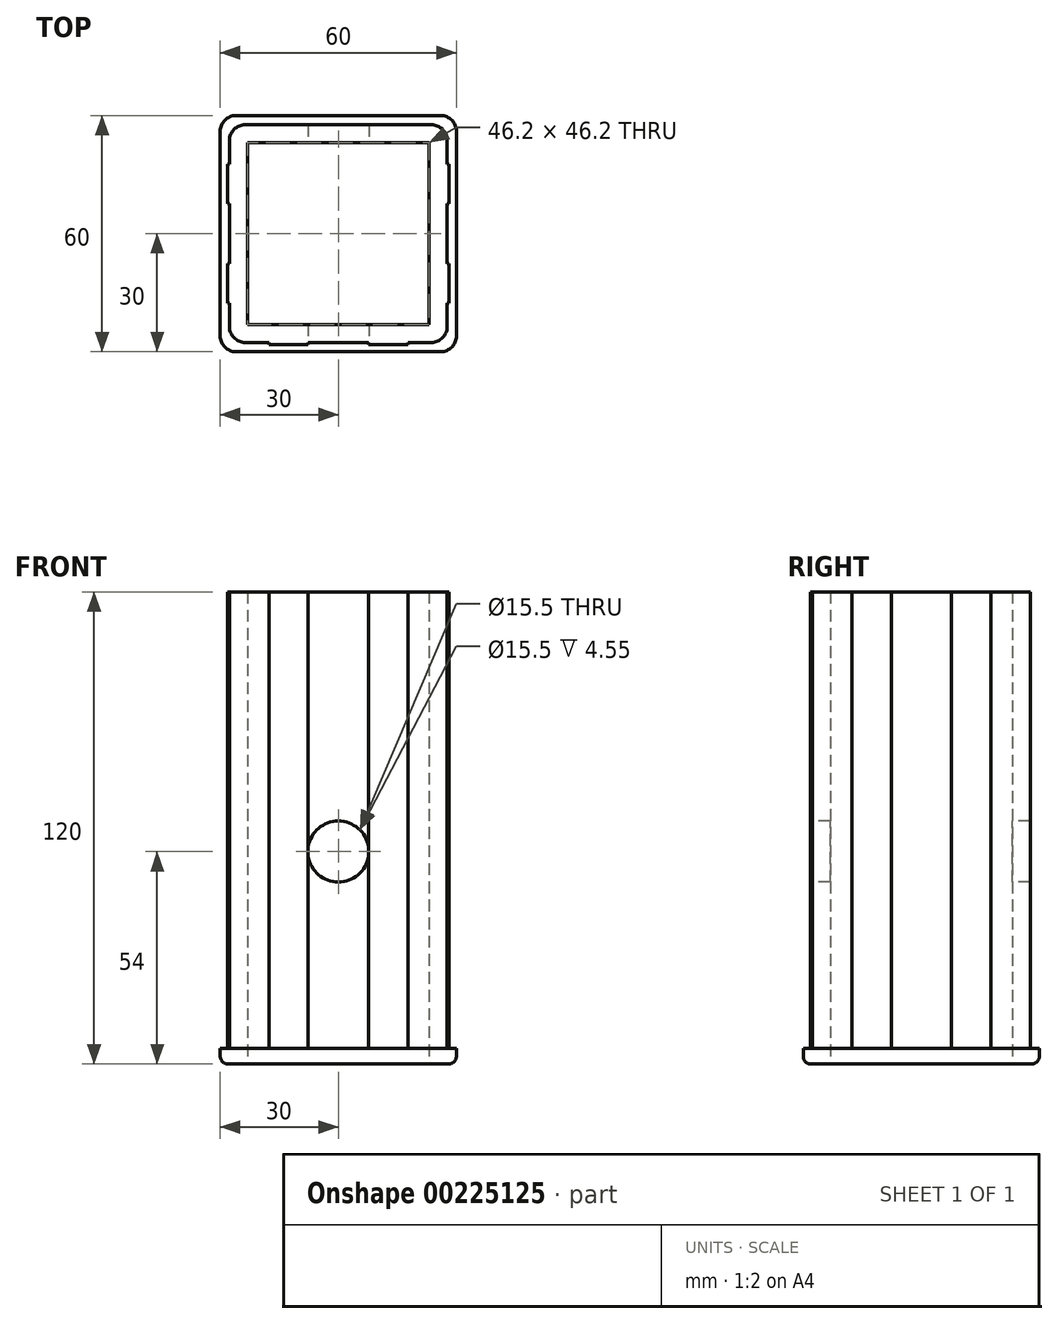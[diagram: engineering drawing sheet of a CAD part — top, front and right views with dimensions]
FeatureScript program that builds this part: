
annotation { "Feature Type Name" : "Feature", "Feature Type Description" : "" }
export const myFeature = defineFeature(function(context is Context, id is Id, definition is map)
    precondition{}
    {
        {
            var Q0;
            Q0=qCreatedBy(makeId("Top.planeOp"),FACE);
            var sketch = newSketch(context, id + "F0", { "sketchPlane" : qUnion([Q0])});
            skLineSegment(sketch, "E0.bottom", {"start": v(30, 30) * mm, "end": v(-30, 30) * mm});
            skLineSegment(sketch, "E0.top", {"start": v(30, -30) * mm, "end": v(-30, -30) * mm});
            skLineSegment(sketch, "E0.left", {"start": v(30, 30) * mm, "end": v(30, -30) * mm});
            skLineSegment(sketch, "E0.right", {"start": v(-30, 30) * mm, "end": v(-30, -30) * mm});
            skPoint(sketch, "E0.middle", {"position": v(0, 0) * mm});
            skLineSegment(sketch, "E1.bottom", {"start": v(23.1, 23.1) * mm, "end": v(-23.1, 23.1) * mm});
            skLineSegment(sketch, "E1.top", {"start": v(23.1, -23.1) * mm, "end": v(-23.1, -23.1) * mm});
            skLineSegment(sketch, "E1.left", {"start": v(23.1, 23.1) * mm, "end": v(23.1, -23.1) * mm});
            skLineSegment(sketch, "E1.right", {"start": v(-23.1, 23.1) * mm, "end": v(-23.1, -23.1) * mm});
            skLineSegment(sketch, "E2.bottom", {"start": v(27.65, 27.65) * mm, "end": v(-27.65, 27.65) * mm});
            skLineSegment(sketch, "E2.top", {"start": v(27.65, -27.65) * mm, "end": v(17.65, -27.65) * mm});
            skLineSegment(sketch, "E2.left", {"start": v(27.65, 27.65) * mm, "end": v(27.65, 17.65) * mm});
            skLineSegment(sketch, "E2.right", {"start": v(-27.65, 27.65) * mm, "end": v(-27.65, 17.65) * mm});
            skLineSegment(sketch, "E3", {"start": v(27.65, 17.65) * mm, "end": v(28.15, 17.65) * mm});
            skLineSegment(sketch, "E4", {"start": v(28.15, 17.65) * mm, "end": v(28.15, 7.65) * mm});
            skLineSegment(sketch, "E5", {"start": v(27.65, 7.65) * mm, "end": v(28.15, 7.65) * mm});
            skLineSegment(sketch, "E6.trimOffspring", {"start": v(27.65, 7.65) * mm, "end": v(27.65, -7.65) * mm});
            skLineSegment(sketch, "E7", {"start": v(27.65, -17.65) * mm, "end": v(28.15, -17.65) * mm});
            skLineSegment(sketch, "E8", {"start": v(28.15, -17.65) * mm, "end": v(28.15, -7.65) * mm});
            skLineSegment(sketch, "E9", {"start": v(28.15, -7.65) * mm, "end": v(27.65, -7.65) * mm});
            skLineSegment(sketch, "E10.trimOffspring", {"start": v(27.65, -17.65) * mm, "end": v(27.65, -27.65) * mm});
            skLineSegment(sketch, "E11", {"start": v(17.65, -27.65) * mm, "end": v(17.65, -28.15) * mm});
            skLineSegment(sketch, "E12", {"start": v(17.65, -28.15) * mm, "end": v(7.65, -28.15) * mm});
            skLineSegment(sketch, "E13", {"start": v(7.65, -28.15) * mm, "end": v(7.65, -27.65) * mm});
            skLineSegment(sketch, "E14", {"start": v(-7.65, -27.65) * mm, "end": v(-7.65, -28.15) * mm});
            skLineSegment(sketch, "E15", {"start": v(-7.65, -28.15) * mm, "end": v(-17.65, -28.15) * mm});
            skLineSegment(sketch, "E16", {"start": v(-17.65, -28.15) * mm, "end": v(-17.65, -27.65) * mm});
            skLineSegment(sketch, "E17", {"start": v(-27.65, -17.65) * mm, "end": v(-28.15, -17.65) * mm});
            skLineSegment(sketch, "E18", {"start": v(-28.15, -17.65) * mm, "end": v(-28.15, -7.65) * mm});
            skLineSegment(sketch, "E19", {"start": v(-28.15, -7.65) * mm, "end": v(-27.65, -7.65) * mm});
            skLineSegment(sketch, "E20", {"start": v(-27.65, 17.65) * mm, "end": v(-28.15, 17.65) * mm});
            skLineSegment(sketch, "E21", {"start": v(-28.15, 17.65) * mm, "end": v(-28.15, 7.65) * mm});
            skLineSegment(sketch, "E22", {"start": v(-28.15, 7.65) * mm, "end": v(-27.65, 7.65) * mm});
            skLineSegment(sketch, "E23.trimOffspring", {"start": v(-27.65, 7.65) * mm, "end": v(-27.65, -7.65) * mm});
            skLineSegment(sketch, "E24.trimOffspring", {"start": v(-27.65, -17.65) * mm, "end": v(-27.65, -27.65) * mm});
            skLineSegment(sketch, "E25.trimOffspring", {"start": v(-17.65, -27.65) * mm, "end": v(-27.65, -27.65) * mm});
            skLineSegment(sketch, "E26.trimOffspring", {"start": v(7.65, -27.65) * mm, "end": v(-7.65, -27.65) * mm});
            skSolve(sketch);
        }
        {
            var Q0;
            Q0=makeQuery(id+"F0.imprint","IMPRINT",FACE,{"disambiguationData":[TD([[makeQuery(id+"F0.imprint","IMPRINT",EDGE,{"derivedFrom":sQuery(id+"F0.wireOp",EDGE,"E1.bottom")}),-1.0]])]});
            extrude(context, id + "F1", {"entities" : qUnion([Q0]), "depth" : 116 * mm});
        }
        {
            var Q0;
            Q0=makeQuery(id+"F0.imprint","IMPRINT",FACE,{"disambiguationData":[TD([[makeQuery(id+"F0.imprint","IMPRINT",EDGE,{"derivedFrom":sQuery(id+"F0.wireOp",EDGE,"E0.bottom")}),1.0]])]});
            var Q1;
            Q1=makeQuery(id+"F0.imprint","IMPRINT",FACE,{"disambiguationData":[TD([[makeQuery(id+"F0.imprint","IMPRINT",EDGE,{"derivedFrom":sQuery(id+"F0.wireOp",EDGE,"E1.bottom")}),-1.0]])]});
            extrude(context, id + "F2", {"entities" : qUnion([Q0, Q1]), "operationType" : NewBodyOperationType.ADD, "oppositeDirection" : true, "depth" : 4 * mm});
        }
        {
            var Q0;
            Q0=makeQuery(id+"F1.opExtrude","SWEPT_EDGE",EDGE,{"disambiguationData":[OSD([sQuery(id+"F0.wireOp",EDGE,"E2.bottom"),sQuery(id+"F0.wireOp",EDGE,"E2.right")])]});
            var Q1;
            Q1=makeQuery(id+"F1.opExtrude","SWEPT_EDGE",EDGE,{"disambiguationData":[OSD([sQuery(id+"F0.wireOp",EDGE,"E24.trimOffspring"),sQuery(id+"F0.wireOp",EDGE,"E25.trimOffspring")])]});
            var Q2;
            Q2=makeQuery(id+"F1.opExtrude","SWEPT_EDGE",EDGE,{"disambiguationData":[OSD([sQuery(id+"F0.wireOp",EDGE,"E2.top"),sQuery(id+"F0.wireOp",EDGE,"E10.trimOffspring")])]});
            var Q3;
            Q3=makeQuery(id+"F1.opExtrude","SWEPT_EDGE",EDGE,{"disambiguationData":[OSD([sQuery(id+"F0.wireOp",EDGE,"E2.bottom"),sQuery(id+"F0.wireOp",EDGE,"E2.left")])]});
            var Q4;
            Q4=makeQuery(id+"F2.opExtrude","SWEPT_EDGE",EDGE,{"disambiguationData":[OSD([sQuery(id+"F0.wireOp",EDGE,"E0.bottom"),sQuery(id+"F0.wireOp",EDGE,"E0.left")])]});
            var Q5;
            Q5=makeQuery(id+"F2.opExtrude","SWEPT_EDGE",EDGE,{"disambiguationData":[OSD([sQuery(id+"F0.wireOp",EDGE,"E0.top"),sQuery(id+"F0.wireOp",EDGE,"E0.left")])]});
            var Q6;
            Q6=makeQuery(id+"F2.opExtrude","SWEPT_EDGE",EDGE,{"disambiguationData":[OSD([sQuery(id+"F0.wireOp",EDGE,"E0.bottom"),sQuery(id+"F0.wireOp",EDGE,"E0.right")])]});
            var Q7;
            Q7=makeQuery(id+"F2.opExtrude","SWEPT_EDGE",EDGE,{"disambiguationData":[OSD([sQuery(id+"F0.wireOp",EDGE,"E0.top"),sQuery(id+"F0.wireOp",EDGE,"E0.right")])]});
            fillet(context, id + "F3", {"entities" : qUnion([Q0, Q1, Q2, Q3, Q4, Q5, Q6, Q7]), "radius" : 4 * mm, "tangentPropagation" : true, "allowEdgeOverflow" : false});
        }
        {
            var Q0;
            Q0=makeQuery(id+"F2.opExtrude","CAP_EDGE",EDGE,{"disambiguationData":[OSD([sQuery(id+"F0.wireOp",EDGE,"E0.left")])],"isStart":false});
            fillet(context, id + "F4", {"entities" : qUnion([Q0]), "radius" : 2 * mm, "tangentPropagation" : true, "allowEdgeOverflow" : false});
        }
        {
            var Q0;
            Q0=qCreatedBy(makeId("Front.planeOp"),FACE);
            cPlane(context, id + "F5", {"entities" : qUnion([Q0]), "cplaneType" : CPlaneType.OFFSET, "offset" : 27.65 * mm, "width" : 150 * mm, "height" : 150 * mm});
        }
        {
            var Q0;
            Q0=qCreatedBy(id+"F5.planeOp",FACE);
            var sketch = newSketch(context, id + "F6", { "sketchPlane" : qUnion([Q0])});
            skCircle(sketch, "E27", {"center": v(0, 50) * mm, "radius": 7.75 * mm});
            skSolve(sketch);
        }
        {
            var Q0;
            Q0=makeQuery(id+"F6.imprint","IMPRINT",FACE,{"disambiguationData":[TD([[makeQuery(id+"F6.imprint","IMPRINT",EDGE,{"derivedFrom":sQuery(id+"F6.wireOp",EDGE,"E27")}),1.0]])]});
            extrude(context, id + "F7", {"entities" : qUnion([Q0]), "operationType" : NewBodyOperationType.REMOVE, "oppositeDirection" : true, "depth" : 80 * mm});
        }
    });
